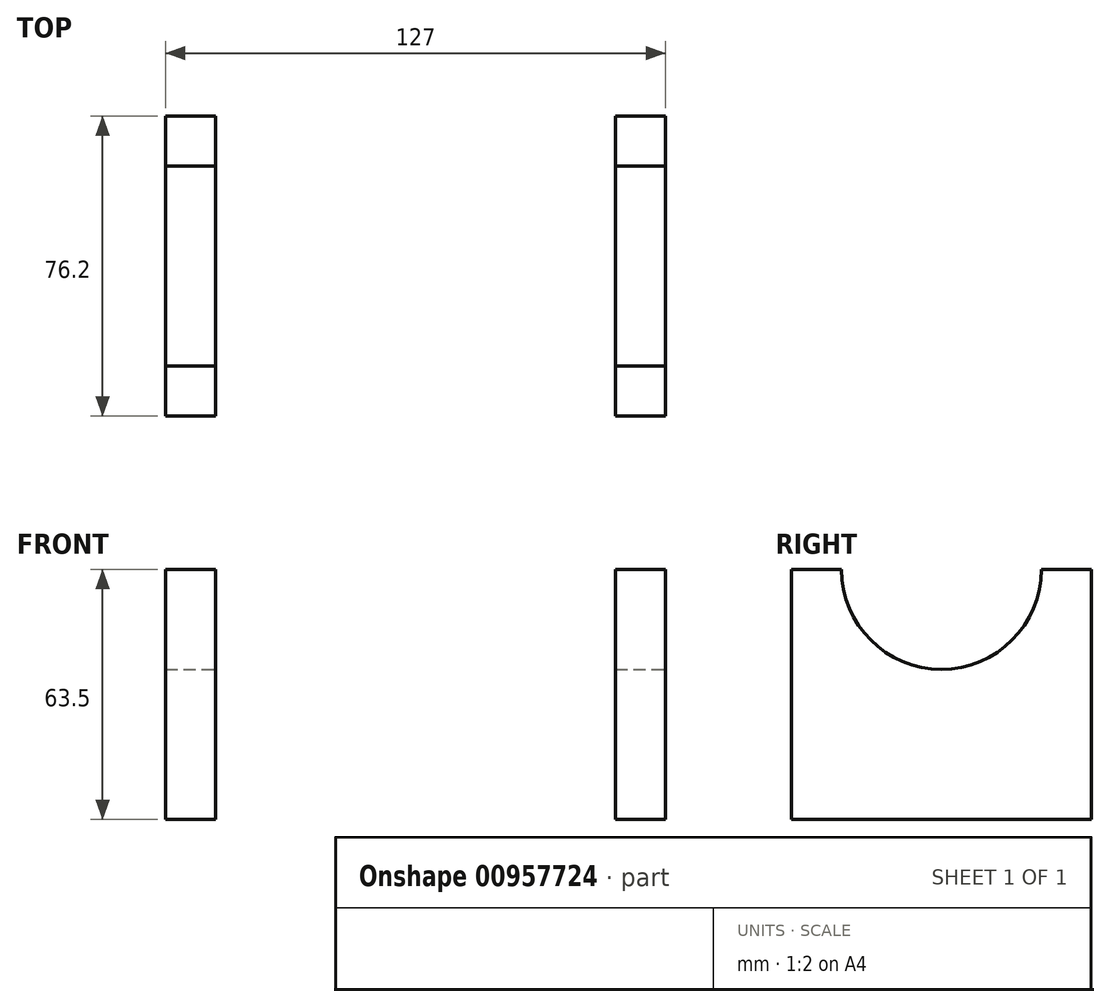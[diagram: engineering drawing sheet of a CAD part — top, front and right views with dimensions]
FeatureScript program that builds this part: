
annotation { "Feature Type Name" : "Feature", "Feature Type Description" : "" }
export const myFeature = defineFeature(function(context is Context, id is Id, definition is map)
    precondition{}
    {
        {
            var Q0;
            Q0=qCreatedBy(makeId("Top.planeOp"),FACE);
            var sketch = newSketch(context, id + "F0", { "sketchPlane" : qUnion([Q0])});
            skLineSegment(sketch, "E0.bottom", {"start": v(63.5, 38.1) * mm, "end": v(-63.5, 38.1) * mm});
            skLineSegment(sketch, "E0.top", {"start": v(63.5, -38.1) * mm, "end": v(-63.5, -38.1) * mm});
            skLineSegment(sketch, "E0.left", {"start": v(63.5, 38.1) * mm, "end": v(63.5, -38.1) * mm});
            skLineSegment(sketch, "E0.right", {"start": v(-63.5, 38.1) * mm, "end": v(-63.5, -38.1) * mm});
            skPoint(sketch, "E0.middle", {"position": v(0, 0) * mm});
            skLineSegment(sketch, "E1", {"start": v(63.5, 38.1) * mm, "end": v(63.5, 0) * mm});
            skLineSegment(sketch, "E2", {"start": v(-63.5, -38.1) * mm, "end": v(0, -38.1) * mm});
            skLineSegment(sketch, "E3", {"start": v(0, -38.1) * mm, "end": v(0, 38.1) * mm, "construction": true});
            skLineSegment(sketch, "E4", {"start": v(63.5, 0) * mm, "end": v(-63.5, 0) * mm, "construction": true});
            skCircle(sketch, "E5", {"center": v(0, 0) * mm, "radius": 15.88 * mm});
            skLineSegment(sketch, "E6", {"start": v(63.5, -38.1) * mm, "end": v(50.8, -38.1) * mm});
            skLineSegment(sketch, "E7", {"start": v(50.8, -38.1) * mm, "end": v(50.8, 38.1) * mm});
            skLineSegment(sketch, "E8.MirrorCS", {"start": v(-63.5, -38.1) * mm, "end": v(-50.8, -38.1) * mm});
            skLineSegment(sketch, "E9.MirrorCS", {"start": v(-50.8, -38.1) * mm, "end": v(-50.8, 38.1) * mm});
            skSolve(sketch);
        }
        {
            var Q0;
            Q0=makeQuery(id+"F0.imprint","IMPRINT",FACE,{"disambiguationData":[TD([[makeQuery(id+"F0.imprint","IMPRINT",EDGE,{"derivedFrom":sQuery(id+"F0.wireOp",EDGE,"E0.top")}),-1.0]])]});
            var Q1;
            {var subQ0=sQuery(id+"F0.wireOp",EDGE,"E0.right");Q1=makeQuery(id+"F0.imprint","IMPRINT",FACE,{"disambiguationData":[TD([[makeQuery(id+"F0.imprint","IMPRINT",EDGE,{"derivedFrom":subQ0}),1.0]])]});}
            var Q2;
            Q2=makeQuery(id+"F0.imprint","IMPRINT",FACE,{"disambiguationData":[TD([[makeQuery(id+"F0.imprint","IMPRINT",EDGE,{"derivedFrom":sQuery(id+"F0.wireOp",EDGE,"E0.left")}),-1.0]])]});
            extrude(context, id + "F1", {"entities" : qUnion([Q0, Q1, Q2]), "depth" : 12.7 * mm, "offsetDistance" : 25.4 * mm});
        }
        {
            var Q0;
            {var subQ0=sQuery(id+"F0.wireOp",EDGE,"E0.right");Q0=makeQuery(id+"F0.imprint","IMPRINT",FACE,{"disambiguationData":[TD([[makeQuery(id+"F0.imprint","IMPRINT",EDGE,{"derivedFrom":subQ0}),1.0]])]});}
            var Q1;
            Q1=makeQuery(id+"F0.imprint","IMPRINT",FACE,{"disambiguationData":[TD([[makeQuery(id+"F0.imprint","IMPRINT",EDGE,{"derivedFrom":sQuery(id+"F0.wireOp",EDGE,"E0.left")}),-1.0]])]});
            extrude(context, id + "F2", {"entities" : qUnion([Q0, Q1]), "operationType" : NewBodyOperationType.ADD, "depth" : 63.5 * mm, "offsetDistance" : 25.4 * mm});
        }
        {
            var Q0;
            {var subQ0=sQuery(id+"F0.wireOp",EDGE,"E1");var subQ1=sQuery(id+"F0.wireOp",EDGE,"E0.left");Q0=makeQuery(id+"F2.boolean.opBoolean","MERGE",FACE,{"derivedFrom":[makeQuery(id+"F1.opExtrude","SWEPT_FACE",FACE,{"disambiguationData":[OSD([subQ1,subQ0])]}),makeQuery(id+"F2.opExtrude","SWEPT_FACE",FACE,{"disambiguationData":[OSD([subQ1,subQ0])]})]});}
            var sketch = newSketch(context, id + "F3", { "sketchPlane" : qUnion([Q0])});
            skCircle(sketch, "E10", {"center": v(0, 63.5) * mm, "radius": 25.4 * mm});
            skSolve(sketch);
        }
        {
            var Q0;
            {var subQ0=sQuery(id+"F3.wireOp",EDGE,"E10");var subQ1=makeQuery(id+"F2.opExtrude","CAP_EDGE",EDGE,{"disambiguationData":[OSD([sQuery(id+"F0.wireOp",EDGE,"E0.left"),sQuery(id+"F0.wireOp",EDGE,"E1")])],"isStart":false});var subQ2=makeQuery(id+"F3.imprint","INTERSECT",VERTEX,{"disambiguationData":[OD(0.0)],"derivedFrom":[subQ1,subQ0]});Q0=makeQuery(id+"F3.imprint","IMPRINT",FACE,{"disambiguationData":[TD([[makeQuery(id+"F3.imprint","IMPRINT",EDGE,{"disambiguationData":[TD([[subQ2,1.0]])],"derivedFrom":subQ0}),1.0]])]});}
            extrude(context, id + "F4", {"entities" : qUnion([Q0]), "operationType" : NewBodyOperationType.REMOVE, "endBound" : BoundingType.THROUGH_ALL, "oppositeDirection" : true, "depth" : 25.4 * mm, "offsetDistance" : 25.4 * mm});
        }
    });
